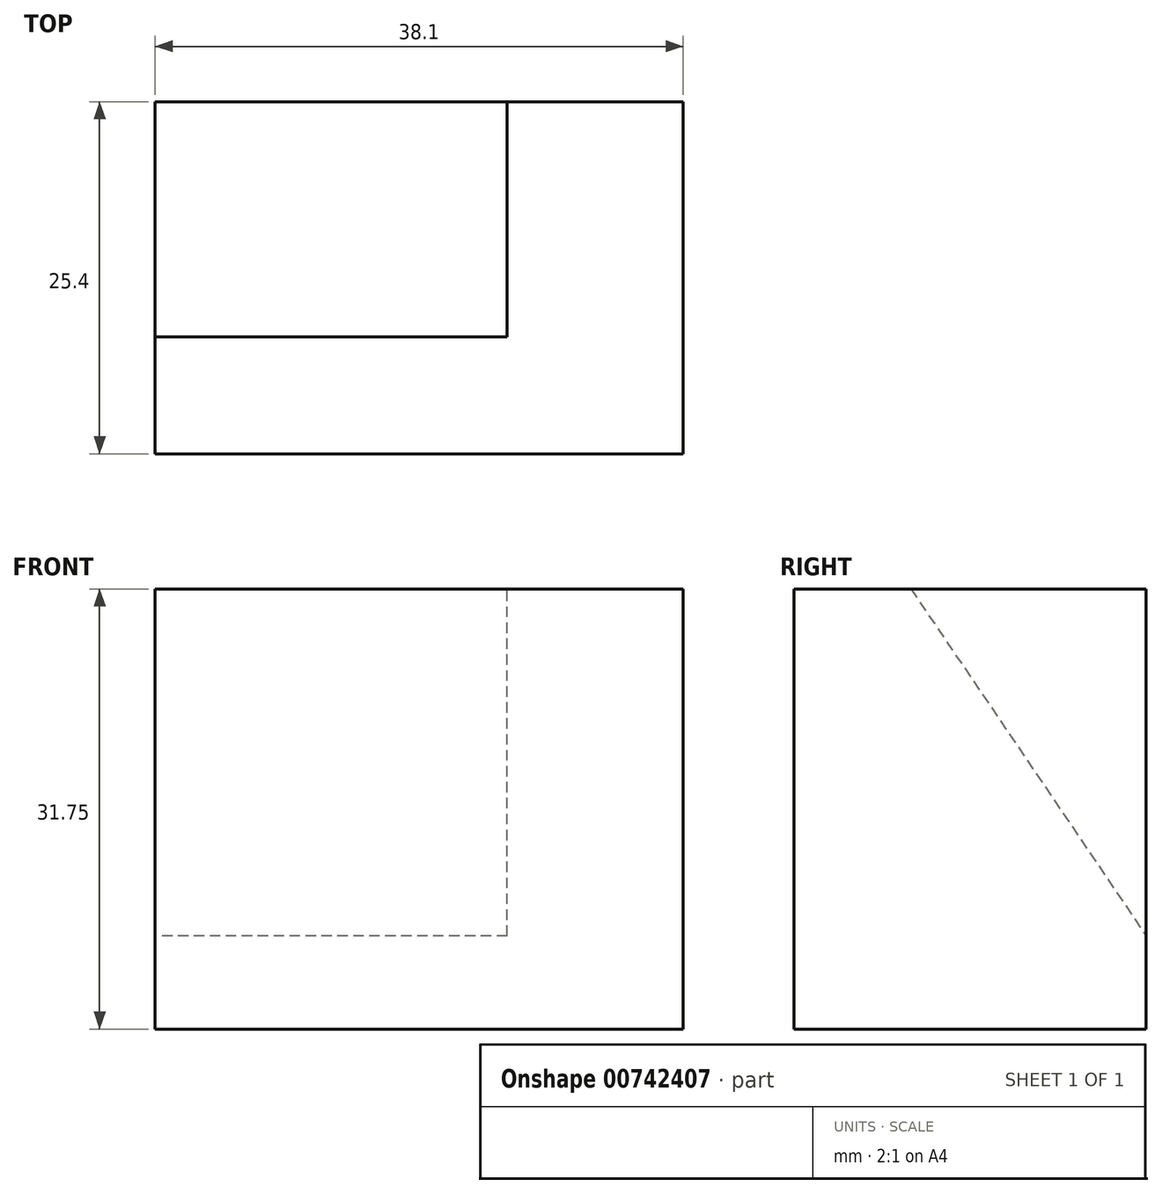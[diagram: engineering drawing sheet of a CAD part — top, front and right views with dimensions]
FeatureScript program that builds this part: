
annotation { "Feature Type Name" : "Feature", "Feature Type Description" : "" }
export const myFeature = defineFeature(function(context is Context, id is Id, definition is map)
    precondition{}
    {
        {
            var Q0;
            Q0=qCreatedBy(makeId("Front.planeOp"),FACE);
            var sketch = newSketch(context, id + "F0", { "sketchPlane" : qUnion([Q0])});
            skLineSegment(sketch, "E0", {"start": v(0, 31.75) * mm, "end": v(0, 0) * mm});
            skLineSegment(sketch, "E1", {"start": v(0, 0) * mm, "end": v(38.1, 0) * mm});
            skLineSegment(sketch, "E2", {"start": v(38.1, 0) * mm, "end": v(38.1, 31.75) * mm});
            skLineSegment(sketch, "E3", {"start": v(38.1, 31.75) * mm, "end": v(0, 31.75) * mm});
            skSolve(sketch);
        }
        {
            var Q0;
            Q0 = qSketchRegion(id + "F0", true);
            extrude(context, id + "F1", {"entities" : qUnion([Q0]), "depth" : 25.4 * mm, "offsetDistance" : 25.4 * mm});
        }
        {
            var Q0;
            Q0=qCreatedBy(makeId("Right.planeOp"),FACE);
            var sketch = newSketch(context, id + "F2", { "sketchPlane" : qUnion([Q0])});
            skLineSegment(sketch, "E4", {"start": v(-17.2, 32.08) * mm, "end": v(0, 6.72) * mm});
            skLineSegment(sketch, "E5", {"start": v(0, 6.72) * mm, "end": v(0, 31.7) * mm});
            skLineSegment(sketch, "E6", {"start": v(0, 31.7) * mm, "end": v(-17.2, 32.08) * mm});
            skSolve(sketch);
        }
        {
            var Q0;
            Q0 = qSketchRegion(id + "F2", true);
            extrude(context, id + "F3", {"entities" : qUnion([Q0]), "operationType" : NewBodyOperationType.REMOVE, "depth" : 25.4 * mm, "offsetDistance" : 25.4 * mm});
        }
        {
            var Q0;
            Q0=makeQuery(id+"F3.boolean.opBoolean","COPY",FACE,{"derivedFrom":makeQuery(id+"F3.opExtrude","SWEPT_FACE",FACE,{"disambiguationData":[OSD([sQuery(id+"F2.wireOp",EDGE,"E6")])]})});
            extrude(context, id + "F4", {"entities" : qUnion([Q0]), "operationType" : NewBodyOperationType.REMOVE, "endBound" : BoundingType.THROUGH_ALL, "oppositeDirection" : true, "depth" : 25.4 * mm, "offsetDistance" : 25.4 * mm});
        }
    });
